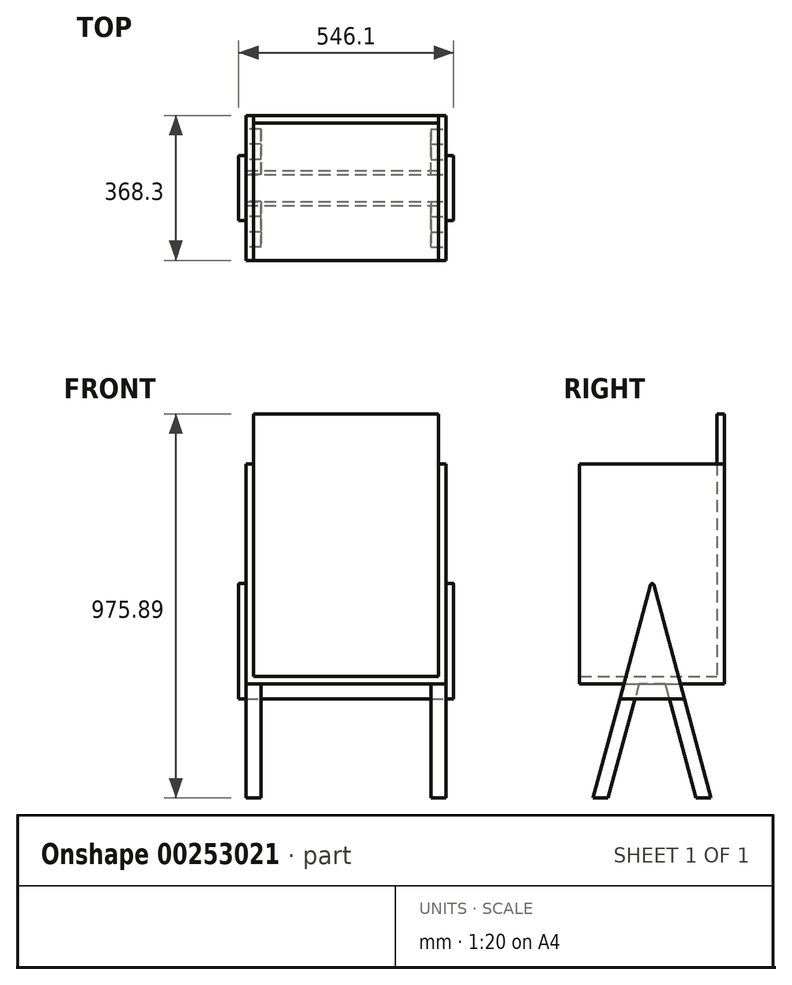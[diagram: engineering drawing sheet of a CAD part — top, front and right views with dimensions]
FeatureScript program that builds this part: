
annotation { "Feature Type Name" : "Feature", "Feature Type Description" : "" }
export const myFeature = defineFeature(function(context is Context, id is Id, definition is map)
    precondition{}
    {
        {
            var Q0;
            Q0=qCreatedBy(makeId("Right.planeOp"),FACE);
            var sketch = newSketch(context, id + "F0", { "sketchPlane" : qUnion([Q0])});
            skLineSegment(sketch, "E0.bottom", {"start": v(-239.65, 461.5) * mm, "end": v(128.65, 461.5) * mm});
            skLineSegment(sketch, "E0.top", {"start": v(-239.65, -97.3) * mm, "end": v(128.65, -97.3) * mm});
            skLineSegment(sketch, "E0.left", {"start": v(-239.65, 461.5) * mm, "end": v(-239.65, -97.3) * mm});
            skLineSegment(sketch, "E0.right", {"start": v(128.65, 461.5) * mm, "end": v(128.65, -97.3) * mm});
            skSolve(sketch);
        }
        {
            var Q0;
            Q0=makeQuery(id+"F0.imprint","IMPRINT",FACE,{"disambiguationData":[TD([[makeQuery(id+"F0.imprint","IMPRINT",EDGE,{"derivedFrom":sQuery(id+"F0.wireOp",EDGE,"E0.bottom")}),-1.0]])]});
            extrude(context, id + "F1", {"entities" : qUnion([Q0]), "depth" : 508 * mm});
        }
        {
            var Q0;
            Q0=makeQuery(id+"F1.opExtrude","SWEPT_FACE",FACE,{"disambiguationData":[OSD([sQuery(id+"F0.wireOp",EDGE,"E0.bottom")])]});
            var Q1;
            Q1=makeQuery(id+"F1.opExtrude","SWEPT_FACE",FACE,{"disambiguationData":[OSD([sQuery(id+"F0.wireOp",EDGE,"E0.left")])]});
            shell(context, id + "F2", {"entities" : qUnion([Q0, Q1]), "thickness" : 19.05 * mm});
        }
        {
            var Q0;
            Q0=makeQuery(id+"F1.opExtrude","SWEPT_FACE",FACE,{"disambiguationData":[OSD([sQuery(id+"F0.wireOp",EDGE,"E0.bottom")])]});
            var sketch = newSketch(context, id + "F3", { "sketchPlane" : qUnion([Q0])});
            skLineSegment(sketch, "E1.bottom", {"start": v(19.05, 109.6) * mm, "end": v(488.95, 109.6) * mm});
            skLineSegment(sketch, "E1.top", {"start": v(19.05, 128.65) * mm, "end": v(488.95, 128.65) * mm});
            skLineSegment(sketch, "E1.left", {"start": v(19.05, 109.6) * mm, "end": v(19.05, 128.65) * mm});
            skLineSegment(sketch, "E1.right", {"start": v(488.95, 109.6) * mm, "end": v(488.95, 128.65) * mm});
            skSolve(sketch);
        }
        {
            var Q0;
            Q0 = qSketchRegion(id + "F3", true);
            extrude(context, id + "F4", {"entities" : qUnion([Q0]), "operationType" : NewBodyOperationType.ADD, "depth" : 127 * mm});
        }
        {
            var Q0;
            Q0=makeQuery(id+"F1.opExtrude","CAP_FACE",FACE,{"disambiguationData":[OSD([sQuery(id+"F0.wireOp",EDGE,"E0.bottom"),sQuery(id+"F0.wireOp",EDGE,"E0.top"),sQuery(id+"F0.wireOp",EDGE,"E0.left"),sQuery(id+"F0.wireOp",EDGE,"E0.right")])],"isStart":false});
            var sketch = newSketch(context, id + "F5", { "sketchPlane" : qUnion([Q0])});
            skLineSegment(sketch, "E2", {"start": v(-55.5, -97.3) * mm, "end": v(-55.5, 29.7) * mm, "construction": true});
            skLineSegment(sketch, "E3", {"start": v(-55.5, 29.7) * mm, "end": v(-167.26, -387.39) * mm, "construction": true});
            skLineSegment(sketch, "E4", {"start": v(-55.5, 29.7) * mm, "end": v(56.26, -387.39) * mm, "construction": true});
            skLineSegment(sketch, "E5", {"start": v(-21.47, -97.3) * mm, "end": v(56.26, -387.39) * mm});
            skLineSegment(sketch, "E6", {"start": v(94.36, -387.39) * mm, "end": v(16.63, -97.3) * mm});
            skLineSegment(sketch, "E7", {"start": v(56.26, -387.39) * mm, "end": v(94.36, -387.39) * mm});
            skLineSegment(sketch, "E8", {"start": v(16.63, -97.3) * mm, "end": v(-21.47, -97.3) * mm});
            skLineSegment(sketch, "E9.MirrorCS", {"start": v(-205.36, -387.39) * mm, "end": v(-127.63, -97.3) * mm});
            skLineSegment(sketch, "E10.MirrorCS", {"start": v(-127.63, -97.3) * mm, "end": v(-89.53, -97.3) * mm});
            skLineSegment(sketch, "E11.MirrorCS", {"start": v(-167.26, -387.39) * mm, "end": v(-205.36, -387.39) * mm});
            skLineSegment(sketch, "E12", {"start": v(-89.53, -97.3) * mm, "end": v(-167.26, -387.39) * mm});
            skSolve(sketch);
        }
        {
            var Q0;
            Q0 = qSketchRegion(id + "F5", true);
            extrude(context, id + "F6", {"entities" : qUnion([Q0]), "oppositeDirection" : true, "depth" : 38.1 * mm});
        }
        {
            var Q0;
            Q0=makeQuery(id+"F1.opExtrude","CAP_FACE",FACE,{"disambiguationData":[OSD([sQuery(id+"F0.wireOp",EDGE,"E0.bottom"),sQuery(id+"F0.wireOp",EDGE,"E0.top"),sQuery(id+"F0.wireOp",EDGE,"E0.left"),sQuery(id+"F0.wireOp",EDGE,"E0.right")])],"isStart":true});
            var sketch = newSketch(context, id + "F7", { "sketchPlane" : qUnion([Q0])});
            skLineSegment(sketch, "E13.0.0", {"start": v(-94.36, -387.39) * mm, "end": v(-56.26, -387.39) * mm});
            skLineSegment(sketch, "E13.0.1", {"start": v(-56.26, -387.39) * mm, "end": v(21.47, -97.3) * mm});
            skLineSegment(sketch, "E13.0.2", {"start": v(21.47, -97.3) * mm, "end": v(-16.63, -97.3) * mm});
            skLineSegment(sketch, "E13.0.3", {"start": v(-16.63, -97.3) * mm, "end": v(-94.36, -387.39) * mm});
            skLineSegment(sketch, "E13.1.0", {"start": v(89.53, -97.3) * mm, "end": v(167.26, -387.39) * mm});
            skLineSegment(sketch, "E13.1.1", {"start": v(167.26, -387.39) * mm, "end": v(205.36, -387.39) * mm});
            skLineSegment(sketch, "E13.1.2", {"start": v(205.36, -387.39) * mm, "end": v(127.63, -97.3) * mm});
            skLineSegment(sketch, "E13.1.3", {"start": v(127.63, -97.3) * mm, "end": v(89.53, -97.3) * mm});
            skSolve(sketch);
        }
        {
            var Q0;
            Q0 = qSketchRegion(id + "F7", true);
            extrude(context, id + "F8", {"entities" : qUnion([Q0]), "oppositeDirection" : true, "depth" : 38.1 * mm});
        }
        {
            var Q0;
            Q0=makeQuery(id+"F1.opExtrude","CAP_FACE",FACE,{"disambiguationData":[OSD([sQuery(id+"F0.wireOp",EDGE,"E0.bottom"),sQuery(id+"F0.wireOp",EDGE,"E0.top"),sQuery(id+"F0.wireOp",EDGE,"E0.left"),sQuery(id+"F0.wireOp",EDGE,"E0.right")])],"isStart":false});
            var sketch = newSketch(context, id + "F9", { "sketchPlane" : qUnion([Q0])});
            skLineSegment(sketch, "E14.0", {"start": v(-239.65, -97.3) * mm, "end": v(128.65, -97.3) * mm});
            skLineSegment(sketch, "E14.1", {"start": v(-21.47, -97.3) * mm, "end": v(-11.26, -135.4) * mm});
            skLineSegment(sketch, "E14.2", {"start": v(-89.53, -97.3) * mm, "end": v(-99.74, -135.4) * mm});
            skLineSegment(sketch, "E15", {"start": v(-99.74, -135.4) * mm, "end": v(-11.26, -135.4) * mm});
            skPoint(sketch, "E16.orphan", {"position": v(-167.26, -387.39) * mm});
            skPoint(sketch, "E17.orphan", {"position": v(56.26, -387.39) * mm});
            skSolve(sketch);
        }
        {
            var Q0;
            Q0 = qSketchRegion(id + "F9", true);
            var Q1;
            Q1=makeQuery(id+"F1.opExtrude","CAP_FACE",FACE,{"disambiguationData":[OSD([sQuery(id+"F0.wireOp",EDGE,"E0.bottom"),sQuery(id+"F0.wireOp",EDGE,"E0.top"),sQuery(id+"F0.wireOp",EDGE,"E0.left"),sQuery(id+"F0.wireOp",EDGE,"E0.right")])],"isStart":true});
            extrude(context, id + "F10", {"entities" : qUnion([Q0]), "endBound" : BoundingType.UP_TO_SURFACE, "oppositeDirection" : true, "endBoundEntityFace" : qUnion([Q1]), "depth" : 25.4 * mm});
        }
        {
            var Q0;
            Q0=makeQuery(id+"F1.opExtrude","CAP_FACE",FACE,{"disambiguationData":[OSD([sQuery(id+"F0.wireOp",EDGE,"E0.bottom"),sQuery(id+"F0.wireOp",EDGE,"E0.top"),sQuery(id+"F0.wireOp",EDGE,"E0.left"),sQuery(id+"F0.wireOp",EDGE,"E0.right")])],"isStart":true});
            var sketch = newSketch(context, id + "F11", { "sketchPlane" : qUnion([Q0])});
            skLineSegment(sketch, "E18.0", {"start": v(11.26, -135.4) * mm, "end": v(99.74, -135.4) * mm});
            skLineSegment(sketch, "E18.1", {"start": v(-16.63, -97.3) * mm, "end": v(-26.84, -135.4) * mm});
            skLineSegment(sketch, "E18.2", {"start": v(137.84, -135.4) * mm, "end": v(127.63, -97.3) * mm});
            skLineSegment(sketch, "E19", {"start": v(11.26, -135.4) * mm, "end": v(-26.84, -135.4) * mm});
            skLineSegment(sketch, "E20", {"start": v(99.74, -135.4) * mm, "end": v(137.84, -135.4) * mm});
            skLineSegment(sketch, "E21", {"start": v(127.63, -97.3) * mm, "end": v(92.67, 33.17) * mm});
            skLineSegment(sketch, "E22", {"start": v(-16.63, -97.3) * mm, "end": v(55.5, 171.89) * mm});
            skLineSegment(sketch, "E23", {"start": v(55.5, 171.89) * mm, "end": v(92.67, 33.17) * mm});
            skPoint(sketch, "E24.orphan", {"position": v(-94.36, -387.39) * mm});
            skPoint(sketch, "E25.orphan", {"position": v(205.36, -387.39) * mm});
            skSolve(sketch);
        }
        {
            var Q0;
            Q0 = qSketchRegion(id + "F11", true);
            extrude(context, id + "F12", {"entities" : qUnion([Q0]), "depth" : 19.05 * mm});
        }
        {
            var Q0;
            Q0=makeQuery(id+"F1.opExtrude","CAP_FACE",FACE,{"disambiguationData":[OSD([sQuery(id+"F0.wireOp",EDGE,"E0.bottom"),sQuery(id+"F0.wireOp",EDGE,"E0.top"),sQuery(id+"F0.wireOp",EDGE,"E0.left"),sQuery(id+"F0.wireOp",EDGE,"E0.right")])],"isStart":false});
            var sketch = newSketch(context, id + "F13", { "sketchPlane" : qUnion([Q0])});
            skLineSegment(sketch, "E26.0", {"start": v(-55.5, 171.89) * mm, "end": v(26.84, -135.4) * mm});
            skLineSegment(sketch, "E26.1", {"start": v(-99.74, -135.4) * mm, "end": v(-11.26, -135.4) * mm});
            skLineSegment(sketch, "E26.2", {"start": v(26.84, -135.4) * mm, "end": v(-137.84, -135.4) * mm});
            skLineSegment(sketch, "E26.3", {"start": v(-137.84, -135.4) * mm, "end": v(-55.5, 171.89) * mm});
            skSolve(sketch);
        }
        {
            var Q0;
            Q0 = qSketchRegion(id + "F13", true);
            extrude(context, id + "F14", {"entities" : qUnion([Q0]), "depth" : 19.05 * mm});
        }
        {
            var Q0;
            Q0=makeQuery(id+"F14.opExtrude","SWEPT_EDGE",EDGE,{"disambiguationData":[OSD([sQuery(id+"F13.wireOp",EDGE,"E26.0"),sQuery(id+"F13.wireOp",EDGE,"E26.3")])]});
            fillet(context, id + "F15", {"entities" : qUnion([Q0]), "radius" : 5.08 * mm, "tangentPropagation" : true, "allowEdgeOverflow" : false});
        }
        {
            var Q0;
            Q0=makeQuery(id+"F12.opExtrude","SWEPT_EDGE",EDGE,{"disambiguationData":[OSD([sQuery(id+"F11.wireOp",EDGE,"E22"),sQuery(id+"F11.wireOp",EDGE,"E23")])]});
            fillet(context, id + "F16", {"entities" : qUnion([Q0]), "radius" : 5.08 * mm, "tangentPropagation" : true, "allowEdgeOverflow" : false});
        }
    });
